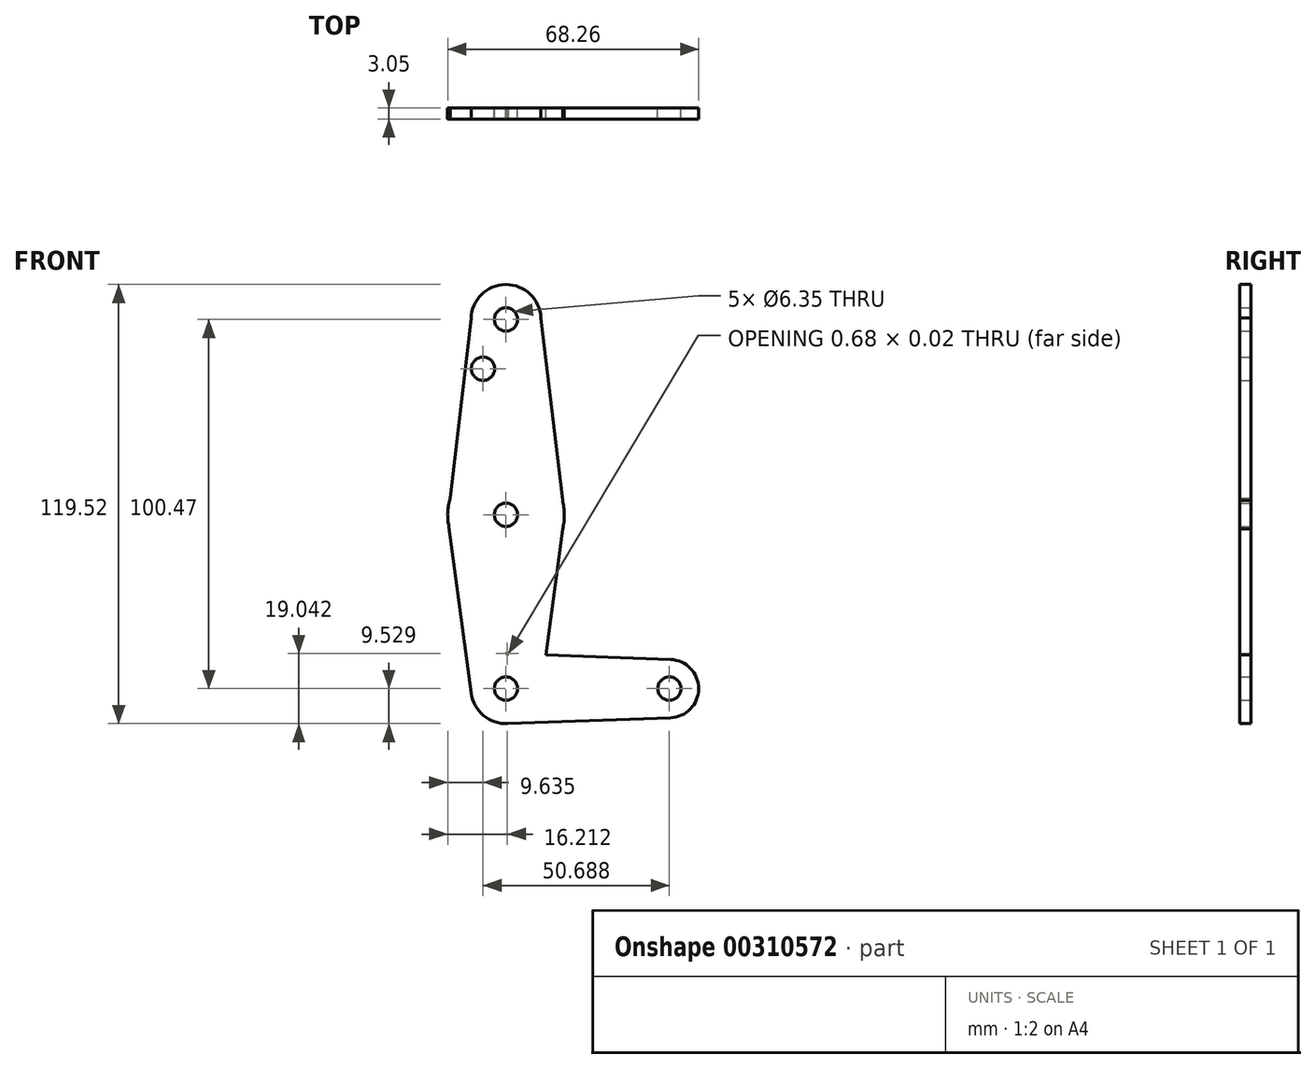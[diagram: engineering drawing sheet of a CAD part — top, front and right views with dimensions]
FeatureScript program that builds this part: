
annotation { "Feature Type Name" : "Feature", "Feature Type Description" : "" }
export const myFeature = defineFeature(function(context is Context, id is Id, definition is map)
    precondition{}
    {
        {
            var Q0;
            Q0=qCreatedBy(makeId("Front.planeOp"),FACE);
            var sketch = newSketch(context, id + "F0", { "sketchPlane" : qUnion([Q0])});
            skLineSegment(sketch, "E0", {"start": v(-106.7, 87.77) * mm, "end": v(-106.7, -26.53) * mm});
            skLineSegment(sketch, "E1", {"start": v(-106.7, -26.53) * mm, "end": v(-62.26, -26.53) * mm});
            skCircle(sketch, "E2", {"center": v(-106.7, 73.94) * mm, "radius": 9.53 * mm});
            skCircle(sketch, "E3", {"center": v(-106.7, -26.53) * mm, "radius": 9.53 * mm});
            skCircle(sketch, "E4", {"center": v(-62.26, -26.53) * mm, "radius": 7.94 * mm});
            skCircle(sketch, "E5", {"center": v(-106.7, 20.8) * mm, "radius": 15.88 * mm});
            skLineSegment(sketch, "E6", {"start": v(-116.23, 74.17) * mm, "end": v(-122.56, 19.95) * mm});
            skLineSegment(sketch, "E7", {"start": v(-122.56, 19.95) * mm, "end": v(-116.15, -27.8) * mm});
            skLineSegment(sketch, "E8", {"start": v(-97.2, 74.36) * mm, "end": v(-90.83, 20.54) * mm});
            skLineSegment(sketch, "E9", {"start": v(-90.83, 20.54) * mm, "end": v(-97.1, -26.53) * mm});
            skLineSegment(sketch, "E10", {"start": v(-106.7, -17) * mm, "end": v(-61.97, -18.6) * mm});
            skLineSegment(sketch, "E11", {"start": v(-106.46, -36.05) * mm, "end": v(-61.97, -34.46) * mm});
            skCircle(sketch, "E12", {"center": v(-106.7, 73.94) * mm, "radius": 3.17 * mm});
            skCircle(sketch, "E13", {"center": v(-106.7, 20.8) * mm, "radius": 3.18 * mm});
            skCircle(sketch, "E14", {"center": v(-106.7, -26.53) * mm, "radius": 3.18 * mm});
            skCircle(sketch, "E15", {"center": v(-62.26, -26.53) * mm, "radius": 3.18 * mm});
            skCircle(sketch, "E16", {"center": v(-112.94, 60.55) * mm, "radius": 3.18 * mm});
            skSolve(sketch);
        }
        {
            var Q0;
            Q0 = qSketchRegion(id + "F0", true);
            var Q1;
            {var subQ5=sQuery(id+"F0.wireOp",EDGE,"E14");var subQ6=sQuery(id+"F0.wireOp",EDGE,"E1");var subQ7=makeQuery(id+"F0.imprint","INTERSECT",VERTEX,{"derivedFrom":[subQ6,subQ5]});Q1=makeQuery(id+"F0.imprint","IMPRINT",FACE,{"disambiguationData":[TD([[makeQuery(id+"F0.imprint","IMPRINT",EDGE,{"disambiguationData":[TD([[subQ7,-1.0]])],"derivedFrom":subQ6}),1.0]])]});}
            extrude(context, id + "F1", {"entities" : qUnion([Q0, Q1]), "depth" : 3.05 * mm});
        }
    });
